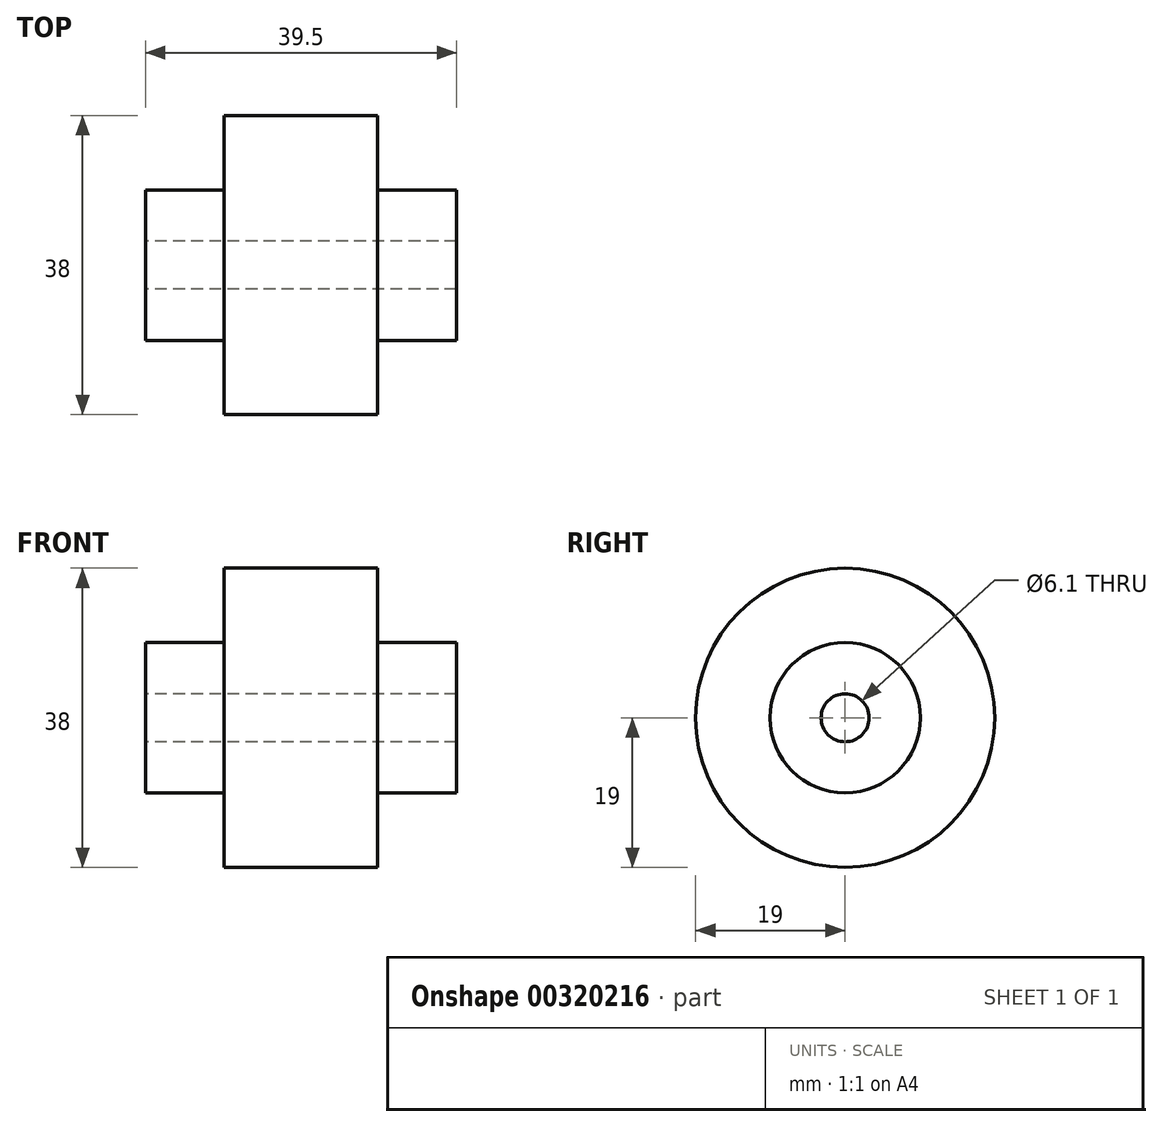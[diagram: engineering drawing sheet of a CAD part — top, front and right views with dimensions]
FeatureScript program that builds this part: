
annotation { "Feature Type Name" : "Feature", "Feature Type Description" : "" }
export const myFeature = defineFeature(function(context is Context, id is Id, definition is map)
    precondition{}
    {
        {
            var Q0;
            Q0=qCreatedBy(makeId("Front.planeOp"),FACE);
            var sketch = newSketch(context, id + "F0", { "sketchPlane" : qUnion([Q0])});
            skLineSegment(sketch, "E0", {"start": v(-31.3, 0) * mm, "end": v(44.47, 0) * mm});
            skLineSegment(sketch, "E1", {"start": v(0, 3.05) * mm, "end": v(39.5, 3.05) * mm});
            skPoint(sketch, "E2.end.orphan", {"position": v(0, 3.05) * mm});
            skLineSegment(sketch, "E3", {"start": v(0, 0) * mm, "end": v(0, 19.1) * mm, "construction": true});
            skLineSegment(sketch, "E4", {"start": v(0, 3.05) * mm, "end": v(0, 9.55) * mm});
            skLineSegment(sketch, "E5", {"start": v(0, 9.55) * mm, "end": v(10, 9.55) * mm});
            skLineSegment(sketch, "E6", {"start": v(39.5, 9.55) * mm, "end": v(39.5, 3.05) * mm});
            skLineSegment(sketch, "E7", {"start": v(10, 9.55) * mm, "end": v(10, 19) * mm});
            skLineSegment(sketch, "E8", {"start": v(10, 19) * mm, "end": v(29.5, 19) * mm});
            skLineSegment(sketch, "E9", {"start": v(29.5, 19) * mm, "end": v(29.5, 9.55) * mm});
            skLineSegment(sketch, "E10.trimOffspring", {"start": v(29.5, 9.55) * mm, "end": v(39.5, 9.55) * mm});
            skSolve(sketch);
        }
        {
            var Q0;
            Q0=makeQuery(id+"F0.imprint","IMPRINT",FACE,{"disambiguationData":[TD([[makeQuery(id+"F0.imprint","IMPRINT",EDGE,{"derivedFrom":sQuery(id+"F0.wireOp",EDGE,"E1")}),1.0]])]});
            var Q1;
            Q1 = qConstructionFilter(qBodyType(qCreatedBy(id + "F0" ,EDGE), BodyType.WIRE), ConstructionObject.NO);
            var Q2;
            Q2=sQuery(id+"F0.wireOp",EDGE,"E0");
            revolve(context, id + "F1", {"entities" : qUnion([Q0]), "surfaceEntities" : qUnion([Q1]), "axis" : qUnion([Q2]), "revolveType" : RevolveType.FULL});
        }
    });
